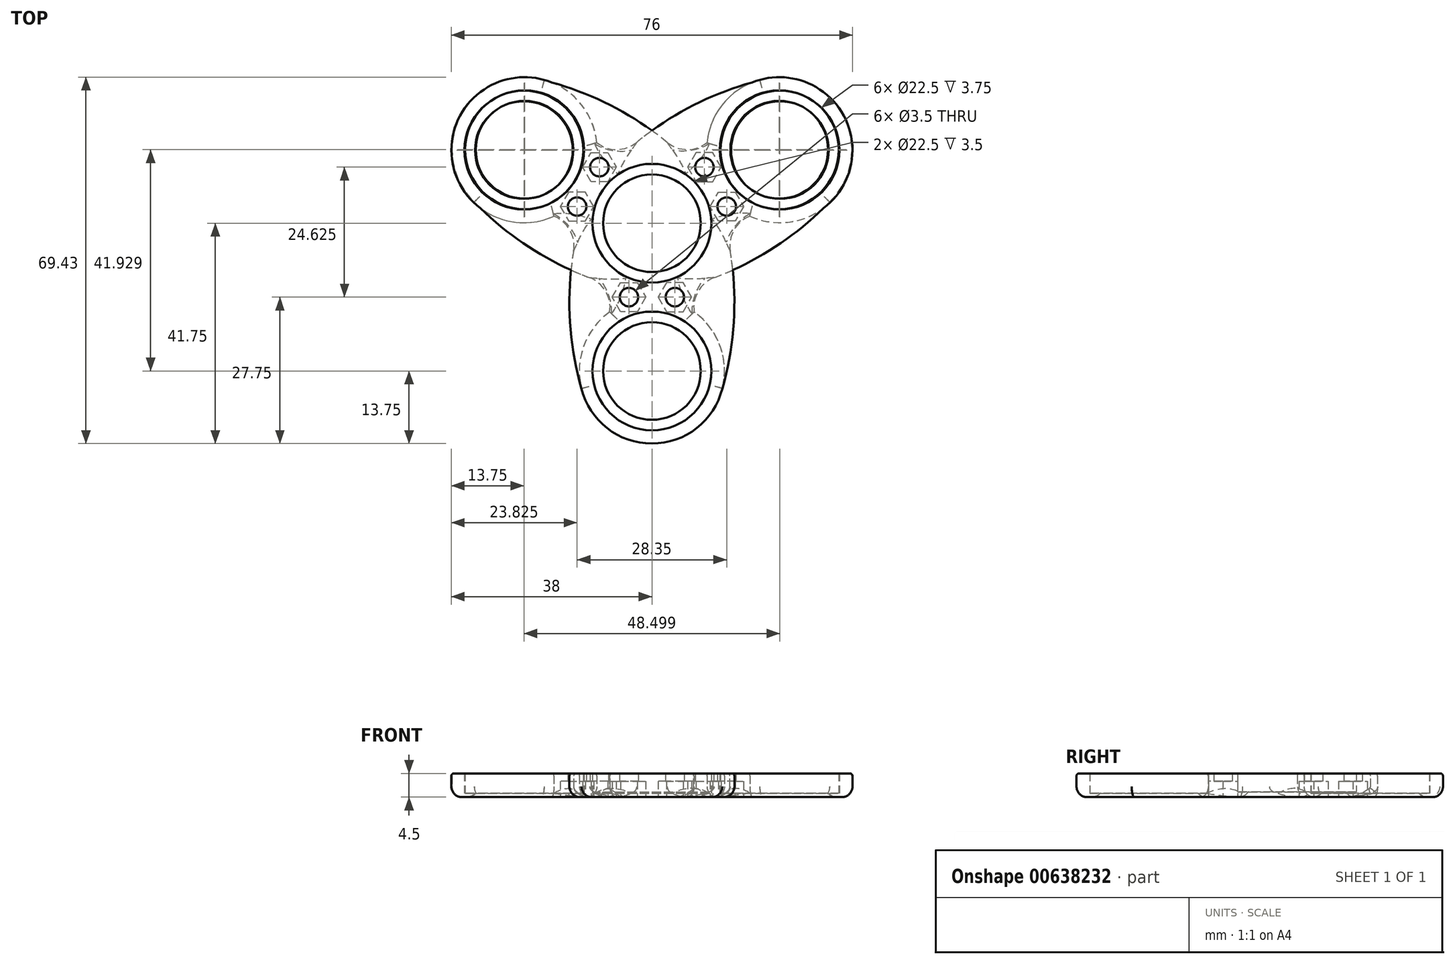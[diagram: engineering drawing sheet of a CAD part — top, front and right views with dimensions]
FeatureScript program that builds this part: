
annotation { "Feature Type Name" : "Feature", "Feature Type Description" : "" }
export const myFeature = defineFeature(function(context is Context, id is Id, definition is map)
    precondition{}
    {
        {
            assignVariable(context, id + "F0", {"name" : "OuterBearingHeight", "anyValue" : 7});
        }
        {
            assignVariable(context, id + "F1", {"name" : "CenterBearingHeight", "anyValue" : 7});
        }
        {
            var Q0;
            Q0=qCreatedBy(makeId("Top.planeOp"),FACE);
            var sketch = newSketch(context, id + "F2", { "sketchPlane" : qUnion([Q0])});
            skCircle(sketch, "E0", {"center": v(0, 0) * mm, "radius": 11.25 * mm});
            skCircle(sketch, "E1", {"center": v(0, 0) * mm, "radius": 9.25 * mm});
            skCircle(sketch, "E2", {"center": v(0, -28) * mm, "radius": 11.25 * mm});
            skCircle(sketch, "E3", {"center": v(0, -28) * mm, "radius": 9.25 * mm});
            skCircle(sketch, "E4", {"center": v(0, 0) * mm, "radius": 13.75 * mm});
            skCircle(sketch, "E5", {"center": v(0, -28) * mm, "radius": 13.75 * mm});
            skArc(sketch, "E6", {"start": v(-13.75, 0) * mm, "mid": v(-15.62, -16.3) * mm, "end": v(-13, -32.48) * mm});
            skArc(sketch, "E7", {"start": v(6.75, -11.98) * mm, "mid": v(7.03, -14.49) * mm, "end": v(8, -16.82) * mm});
            skPoint(sketch, "E8.center", {"position": v(0.04, 0.07) * mm});
            skCircle(sketch, "E9.cCircle", {"center": v(-4.35, -14) * mm, "radius": 2.75 * mm, "construction": true});
            skLineSegment(sketch, "E9.0", {"start": v(-2.76, -16.75) * mm, "end": v(-5.94, -16.75) * mm});
            skLineSegment(sketch, "E9.1", {"start": v(-5.94, -16.75) * mm, "end": v(-7.53, -14) * mm});
            skLineSegment(sketch, "E9.2", {"start": v(-7.53, -14) * mm, "end": v(-5.94, -11.25) * mm});
            skLineSegment(sketch, "E9.3", {"start": v(-5.94, -11.25) * mm, "end": v(-2.76, -11.25) * mm});
            skLineSegment(sketch, "E9.4", {"start": v(-2.76, -11.25) * mm, "end": v(-1.18, -14) * mm});
            skLineSegment(sketch, "E9.5", {"start": v(-1.18, -14) * mm, "end": v(-2.76, -16.75) * mm});
            skPoint(sketch, "E9.0.midPoint", {"position": v(-4.35, -16.75) * mm});
            skLineSegment(sketch, "E10", {"start": v(-4.35, -14) * mm, "end": v(-4.35, -13.04) * mm, "construction": true});
            skLineSegment(sketch, "E11", {"start": v(-4.35, -14) * mm, "end": v(-4.35, -14.96) * mm, "construction": true});
            skLineSegment(sketch, "E12", {"start": v(-4.35, -14) * mm, "end": v(-15.62, -14) * mm, "construction": true});
            skLineSegment(sketch, "E13", {"start": v(-4.35, -14) * mm, "end": v(6.92, -14) * mm, "construction": true});
            skCircle(sketch, "E14", {"center": v(-4.35, -14) * mm, "radius": 1.75 * mm});
            skArc(sketch, "E15.1.0", {"start": v(6.87, 11.76) * mm, "mid": v(8.9, 13.26) * mm, "end": v(10.44, 15.27) * mm});
            skCircle(sketch, "E15.1.1", {"center": v(24.12, 13.93) * mm, "radius": 13.75 * mm});
            skCircle(sketch, "E15.1.2", {"center": v(24.12, 13.93) * mm, "radius": 11.25 * mm});
            skCircle(sketch, "E15.1.3", {"center": v(24.12, 13.93) * mm, "radius": 9.25 * mm});
            skArc(sketch, "E15.1.4", {"start": v(6.75, -11.98) * mm, "mid": v(21.8, -5.45) * mm, "end": v(34.5, 4.9) * mm});
            skLineSegment(sketch, "E15.1.5", {"start": v(12.59, 5.91) * mm, "end": v(15.76, 5.91) * mm});
            skLineSegment(sketch, "E15.1.6", {"start": v(11, 3.16) * mm, "end": v(12.59, 5.91) * mm});
            skLineSegment(sketch, "E15.1.7", {"start": v(12.59, 0.41) * mm, "end": v(11, 3.16) * mm});
            skLineSegment(sketch, "E15.1.8", {"start": v(15.76, 0.41) * mm, "end": v(12.59, 0.41) * mm});
            skLineSegment(sketch, "E15.1.9", {"start": v(17.35, 3.16) * mm, "end": v(15.76, 0.41) * mm});
            skLineSegment(sketch, "E15.1.10", {"start": v(15.76, 5.91) * mm, "end": v(17.35, 3.16) * mm});
            skCircle(sketch, "E15.1.11", {"center": v(14.18, 3.16) * mm, "radius": 1.75 * mm});
            skArc(sketch, "E15.2.0", {"start": v(-13.75, 0) * mm, "mid": v(-16.06, 1) * mm, "end": v(-18.56, 1.34) * mm});
            skCircle(sketch, "E15.2.1", {"center": v(-24.25, 13.86) * mm, "radius": 13.75 * mm});
            skCircle(sketch, "E15.2.2", {"center": v(-24.25, 13.86) * mm, "radius": 11.25 * mm});
            skCircle(sketch, "E15.2.3", {"center": v(-24.25, 13.86) * mm, "radius": 9.25 * mm});
            skArc(sketch, "E15.2.4", {"start": v(6.87, 11.76) * mm, "mid": v(-6.3, 21.52) * mm, "end": v(-21.63, 27.35) * mm});
            skLineSegment(sketch, "E15.2.5", {"start": v(-11.54, 7.87) * mm, "end": v(-13.12, 10.62) * mm});
            skLineSegment(sketch, "E15.2.6", {"start": v(-8.36, 7.87) * mm, "end": v(-11.54, 7.87) * mm});
            skLineSegment(sketch, "E15.2.7", {"start": v(-6.77, 10.62) * mm, "end": v(-8.36, 7.87) * mm});
            skLineSegment(sketch, "E15.2.8", {"start": v(-8.36, 13.37) * mm, "end": v(-6.77, 10.62) * mm});
            skLineSegment(sketch, "E15.2.9", {"start": v(-11.54, 13.37) * mm, "end": v(-8.36, 13.37) * mm});
            skLineSegment(sketch, "E15.2.10", {"start": v(-13.12, 10.62) * mm, "end": v(-11.54, 13.37) * mm});
            skCircle(sketch, "E15.2.11", {"center": v(-9.95, 10.62) * mm, "radius": 1.75 * mm});
            skPoint(sketch, "E15.center", {"position": v(-0.04, -0.07) * mm});
            skSolve(sketch);
        }
        {
            var Q0;
            {var subQ0=sQuery(id+"F2.wireOp",EDGE,"E9.1");Q0=makeQuery(id+"F2.imprint","IMPRINT",FACE,{"disambiguationData":[TD([[makeQuery(id+"F2.imprint","IMPRINT",EDGE,{"derivedFrom":subQ0}),1.0]])]});}
            var Q1;
            {var subQ5=sQuery(id+"F2.wireOp",EDGE,"E7");Q1=makeQuery(id+"F2.imprint","IMPRINT",FACE,{"disambiguationData":[TD([[makeQuery(id+"F2.imprint","IMPRINT",EDGE,{"derivedFrom":subQ5}),-1.0]])]});}
            var Q2;
            {var subQ0=sQuery(id+"F2.wireOp",EDGE,"E15.1.8");Q2=makeQuery(id+"F2.imprint","IMPRINT",FACE,{"disambiguationData":[TD([[makeQuery(id+"F2.imprint","IMPRINT",EDGE,{"derivedFrom":subQ0}),1.0]])]});}
            var Q3;
            Q3=makeQuery(id+"F2.imprint","IMPRINT",FACE,{"disambiguationData":[TD([[makeQuery(id+"F2.imprint","IMPRINT",EDGE,{"derivedFrom":sQuery(id+"F2.wireOp",EDGE,"E0")}),-1.0]])]});
            var Q4;
            {var subQ1=sQuery(id+"F2.wireOp",EDGE,"E15.1.0");Q4=makeQuery(id+"F2.imprint","IMPRINT",FACE,{"disambiguationData":[TD([[makeQuery(id+"F2.imprint","IMPRINT",EDGE,{"derivedFrom":subQ1}),-1.0]])]});}
            var Q5;
            {var subQ0=sQuery(id+"F2.wireOp",EDGE,"E15.2.8");Q5=makeQuery(id+"F2.imprint","IMPRINT",FACE,{"disambiguationData":[TD([[makeQuery(id+"F2.imprint","IMPRINT",EDGE,{"derivedFrom":subQ0}),1.0]])]});}
            var Q6;
            Q6=makeQuery(id+"F2.imprint","IMPRINT",FACE,{"disambiguationData":[TD([[makeQuery(id+"F2.imprint","IMPRINT",EDGE,{"derivedFrom":sQuery(id+"F2.wireOp",EDGE,"E15.2.2")}),-1.0]])]});
            var Q7;
            Q7=makeQuery(id+"F2.imprint","IMPRINT",FACE,{"disambiguationData":[TD([[makeQuery(id+"F2.imprint","IMPRINT",EDGE,{"derivedFrom":sQuery(id+"F2.wireOp",EDGE,"E15.1.2")}),-1.0]])]});
            var Q8;
            {var subQ1=sQuery(id+"F2.wireOp",EDGE,"E15.2.0");Q8=makeQuery(id+"F2.imprint","IMPRINT",FACE,{"disambiguationData":[TD([[makeQuery(id+"F2.imprint","IMPRINT",EDGE,{"derivedFrom":subQ1}),-1.0]])]});}
            var Q9;
            Q9=makeQuery(id+"F2.imprint","IMPRINT",FACE,{"disambiguationData":[TD([[makeQuery(id+"F2.imprint","IMPRINT",EDGE,{"derivedFrom":sQuery(id+"F2.wireOp",EDGE,"E2")}),-1.0]])]});
            var Q10;
            {var subQ0=sQuery(id+"F2.wireOp",EDGE,"E6");var subQ1=sQuery(id+"F2.wireOp",EDGE,"E5");var subQ2=makeQuery(id+"F2.imprint","INTERSECT",VERTEX,{"disambiguationData":[OD(0.0)],"derivedFrom":[subQ1,subQ0]});Q10=makeQuery(id+"F2.imprint","IMPRINT",FACE,{"disambiguationData":[TD([[makeQuery(id+"F2.imprint","IMPRINT",EDGE,{"disambiguationData":[TD([[subQ2,1.0]])],"derivedFrom":subQ1}),1.0]])]});}
            var Q11;
            {var subQ0=sQuery(id+"F2.wireOp",EDGE,"E15.2.4");var subQ1=sQuery(id+"F2.wireOp",EDGE,"E15.2.1");var subQ2=makeQuery(id+"F2.imprint","INTERSECT",VERTEX,{"disambiguationData":[OD(0.0)],"derivedFrom":[subQ1,subQ0]});Q11=makeQuery(id+"F2.imprint","IMPRINT",FACE,{"disambiguationData":[TD([[makeQuery(id+"F2.imprint","IMPRINT",EDGE,{"disambiguationData":[TD([[subQ2,1.0]])],"derivedFrom":subQ1}),1.0]])]});}
            var Q12;
            {var subQ0=sQuery(id+"F2.wireOp",EDGE,"E15.1.4");var subQ1=sQuery(id+"F2.wireOp",EDGE,"E15.1.1");var subQ2=makeQuery(id+"F2.imprint","INTERSECT",VERTEX,{"disambiguationData":[OD(0.0)],"derivedFrom":[subQ1,subQ0]});Q12=makeQuery(id+"F2.imprint","IMPRINT",FACE,{"disambiguationData":[TD([[makeQuery(id+"F2.imprint","IMPRINT",EDGE,{"disambiguationData":[TD([[subQ2,1.0]])],"derivedFrom":subQ1}),1.0]])]});}
            extrude(context, id + "F3", {"entities" : qUnion([Q0, Q1, Q2, Q3, Q4, Q5, Q6, Q7, Q8, Q9, Q10, Q11, Q12]), "depth" : ((getVariable(context, 'CenterBearingHeight') / 2) + 1) * mm, "offsetDistance" : 25 * mm});
        }
        {
            var Q0;
            Q0=makeQuery(id+"F2.imprint","IMPRINT",FACE,{"disambiguationData":[TD([[makeQuery(id+"F2.imprint","IMPRINT",EDGE,{"derivedFrom":sQuery(id+"F2.wireOp",EDGE,"E15.2.2")}),1.0]])]});
            var Q1;
            Q1=makeQuery(id+"F2.imprint","IMPRINT",FACE,{"disambiguationData":[TD([[makeQuery(id+"F2.imprint","IMPRINT",EDGE,{"derivedFrom":sQuery(id+"F2.wireOp",EDGE,"E15.1.2")}),1.0]])]});
            var Q2;
            Q2=makeQuery(id+"F2.imprint","IMPRINT",FACE,{"disambiguationData":[TD([[makeQuery(id+"F2.imprint","IMPRINT",EDGE,{"derivedFrom":sQuery(id+"F2.wireOp",EDGE,"E2")}),1.0]])]});
            extrude(context, id + "F4", {"entities" : qUnion([Q0, Q1, Q2]), "operationType" : NewBodyOperationType.ADD, "depth" : (((getVariable(context, 'CenterBearingHeight') / 2) + .75) - getVariable(context, 'OuterBearingHeight') / 2) * mm, "offsetDistance" : 25 * mm});
        }
        {
            var Q0;
            {var subQ0=sQuery(id+"F2.wireOp",EDGE,"E9.2");var subQ5=sQuery(id+"F2.wireOp",EDGE,"E4");var subQ6=makeQuery(id+"F2.imprint","INTERSECT",VERTEX,{"derivedFrom":[subQ5,subQ0]});Q0=makeQuery(id+"F2.imprint","IMPRINT",FACE,{"disambiguationData":[TD([[makeQuery(id+"F2.imprint","IMPRINT",EDGE,{"disambiguationData":[TD([[subQ6,-1.0]])],"derivedFrom":subQ5}),-1.0]])]});}
            var Q1;
            {var subQ0=sQuery(id+"F2.wireOp",EDGE,"E9.0");Q1=makeQuery(id+"F2.imprint","IMPRINT",FACE,{"disambiguationData":[TD([[makeQuery(id+"F2.imprint","IMPRINT",EDGE,{"derivedFrom":subQ0}),-1.0]])]});}
            var Q2;
            {var subQ1=sQuery(id+"F2.wireOp",EDGE,"E15.2.8");var subQ5=sQuery(id+"F2.wireOp",EDGE,"E4");var subQ6=makeQuery(id+"F2.imprint","INTERSECT",VERTEX,{"derivedFrom":[subQ5,subQ1]});Q2=makeQuery(id+"F2.imprint","IMPRINT",FACE,{"disambiguationData":[TD([[makeQuery(id+"F2.imprint","IMPRINT",EDGE,{"disambiguationData":[TD([[subQ6,-1.0]])],"derivedFrom":subQ5}),-1.0]])]});}
            var Q3;
            {var subQ0=sQuery(id+"F2.wireOp",EDGE,"E15.2.10");Q3=makeQuery(id+"F2.imprint","IMPRINT",FACE,{"disambiguationData":[TD([[makeQuery(id+"F2.imprint","IMPRINT",EDGE,{"derivedFrom":subQ0}),-1.0]])]});}
            var Q4;
            {var subQ5=sQuery(id+"F2.wireOp",EDGE,"E4");var subQ7=sQuery(id+"F2.wireOp",EDGE,"E15.1.11");var subQ9=makeQuery(id+"F2.imprint","INTERSECT",VERTEX,{"disambiguationData":[OD(0.0)],"derivedFrom":[subQ5,subQ7]});Q4=makeQuery(id+"F2.imprint","IMPRINT",FACE,{"disambiguationData":[TD([[makeQuery(id+"F2.imprint","IMPRINT",EDGE,{"disambiguationData":[TD([[subQ9,1.0]])],"derivedFrom":subQ5}),-1.0]])]});}
            var Q5;
            {var subQ0=sQuery(id+"F2.wireOp",EDGE,"E15.1.10");Q5=makeQuery(id+"F2.imprint","IMPRINT",FACE,{"disambiguationData":[TD([[makeQuery(id+"F2.imprint","IMPRINT",EDGE,{"derivedFrom":subQ0}),-1.0]])]});}
            var Q6;
            {var subQ0=sQuery(id+"F2.wireOp",EDGE,"E15.1.7");Q6=makeQuery(id+"F2.imprint","IMPRINT",FACE,{"disambiguationData":[TD([[makeQuery(id+"F2.imprint","IMPRINT",EDGE,{"derivedFrom":subQ0}),-1.0]])]});}
            var Q7;
            {var subQ0=sQuery(id+"F2.wireOp",EDGE,"E15.2.7");Q7=makeQuery(id+"F2.imprint","IMPRINT",FACE,{"disambiguationData":[TD([[makeQuery(id+"F2.imprint","IMPRINT",EDGE,{"derivedFrom":subQ0}),-1.0]])]});}
            var Q8;
            {var subQ5=sQuery(id+"F2.wireOp",EDGE,"E15.2.11");var subQ7=sQuery(id+"F2.wireOp",EDGE,"E4");var subQ9=makeQuery(id+"F2.imprint","INTERSECT",VERTEX,{"disambiguationData":[OD(1.0)],"derivedFrom":[subQ7,subQ5]});Q8=makeQuery(id+"F2.imprint","IMPRINT",FACE,{"disambiguationData":[TD([[makeQuery(id+"F2.imprint","IMPRINT",EDGE,{"disambiguationData":[TD([[subQ9,-1.0]])],"derivedFrom":subQ7}),-1.0]])]});}
            var Q9;
            {var subQ3=sQuery(id+"F2.wireOp",EDGE,"E4");var subQ7=sQuery(id+"F2.wireOp",EDGE,"E15.1.11");var subQ9=makeQuery(id+"F2.imprint","INTERSECT",VERTEX,{"disambiguationData":[OD(1.0)],"derivedFrom":[subQ3,subQ7]});Q9=makeQuery(id+"F2.imprint","IMPRINT",FACE,{"disambiguationData":[TD([[makeQuery(id+"F2.imprint","IMPRINT",EDGE,{"disambiguationData":[TD([[subQ9,-1.0]])],"derivedFrom":subQ3}),-1.0]])]});}
            var Q10;
            {var subQ0=sQuery(id+"F2.wireOp",EDGE,"E9.3");Q10=makeQuery(id+"F2.imprint","IMPRINT",FACE,{"disambiguationData":[TD([[makeQuery(id+"F2.imprint","IMPRINT",EDGE,{"derivedFrom":subQ0}),-1.0]])]});}
            var Q11;
            {var subQ5=sQuery(id+"F2.wireOp",EDGE,"E14");var subQ7=sQuery(id+"F2.wireOp",EDGE,"E4");var subQ8=makeQuery(id+"F2.imprint","INTERSECT",VERTEX,{"disambiguationData":[OD(1.0)],"derivedFrom":[subQ7,subQ5]});Q11=makeQuery(id+"F2.imprint","IMPRINT",FACE,{"disambiguationData":[TD([[makeQuery(id+"F2.imprint","IMPRINT",EDGE,{"disambiguationData":[TD([[subQ8,-1.0]])],"derivedFrom":subQ7}),-1.0]])]});}
            extrude(context, id + "F5", {"entities" : qUnion([Q0, Q1, Q2, Q3, Q4, Q5, Q6, Q7, Q8, Q9, Q10, Q11]), "operationType" : NewBodyOperationType.ADD, "depth" : ((getVariable(context, 'CenterBearingHeight') / 2) + 1) * mm, "offsetDistance" : 25 * mm, "hasSecondDirection" : true, "secondDirectionOppositeDirection" : false, "secondDirectionDepth" : 3 * mm});
        }
        {
            var Q0;
            Q0=makeQuery(id+"F2.imprint","IMPRINT",FACE,{"disambiguationData":[TD([[makeQuery(id+"F2.imprint","IMPRINT",EDGE,{"derivedFrom":sQuery(id+"F2.wireOp",EDGE,"E0")}),1.0]])]});
            extrude(context, id + "F6", {"entities" : qUnion([Q0]), "operationType" : NewBodyOperationType.ADD, "depth" : 1 * mm, "offsetDistance" : 25 * mm});
        }
        {
            var Q0;
            Q0=makeQuery(id+"F3.opExtrude","CAP_EDGE",EDGE,{"disambiguationData":[OSD([sQuery(id+"F2.wireOp",EDGE,"E15.1.1")])],"isStart":true});
            var Q1;
            Q1=makeQuery(id+"F3.opExtrude","CAP_EDGE",EDGE,{"disambiguationData":[OSD([sQuery(id+"F2.wireOp",EDGE,"E15.1.4")])],"isStart":true});
            var Q2;
            Q2=makeQuery(id+"F3.opExtrude","CAP_EDGE",EDGE,{"disambiguationData":[OSD([sQuery(id+"F2.wireOp",EDGE,"E7")])],"isStart":true});
            var Q3;
            Q3=makeQuery(id+"F3.opExtrude","CAP_EDGE",EDGE,{"disambiguationData":[OSD([sQuery(id+"F2.wireOp",EDGE,"E5")])],"isStart":true});
            var Q4;
            Q4=makeQuery(id+"F3.opExtrude","CAP_EDGE",EDGE,{"disambiguationData":[OSD([sQuery(id+"F2.wireOp",EDGE,"E6")])],"isStart":true});
            var Q5;
            Q5=makeQuery(id+"F3.opExtrude","CAP_EDGE",EDGE,{"disambiguationData":[OSD([sQuery(id+"F2.wireOp",EDGE,"E15.2.0")])],"isStart":true});
            var Q6;
            Q6=makeQuery(id+"F3.opExtrude","CAP_EDGE",EDGE,{"disambiguationData":[OSD([sQuery(id+"F2.wireOp",EDGE,"E15.2.1")])],"isStart":true});
            var Q7;
            Q7=makeQuery(id+"F3.opExtrude","CAP_EDGE",EDGE,{"disambiguationData":[OSD([sQuery(id+"F2.wireOp",EDGE,"E15.2.4")])],"isStart":true});
            var Q8;
            Q8=makeQuery(id+"F3.opExtrude","CAP_EDGE",EDGE,{"disambiguationData":[OSD([sQuery(id+"F2.wireOp",EDGE,"E15.1.0")])],"isStart":true});
            var Q9;
            {var subQ0=sQuery(id+"F2.wireOp",EDGE,"E4");Q9=makeQuery(id+"F3.opExtrude","CAP_EDGE",EDGE,{"disambiguationData":[OSD([subQ0]),TDD([makeQuery(id+"F2.imprint","IMPRINT",EDGE,{"disambiguationData":[TD([[makeQuery(id+"F2.imprint","INTERSECT",VERTEX,{"derivedFrom":[subQ0,sQuery(id+"F2.wireOp",EDGE,"E15.1.0")]}),-1.0]])],"derivedFrom":subQ0})])],"isStart":true});}
            var Q10;
            {var subQ0=sQuery(id+"F2.wireOp",EDGE,"E4");Q10=makeQuery(id+"F3.opExtrude","CAP_EDGE",EDGE,{"disambiguationData":[OSD([subQ0]),TDD([makeQuery(id+"F2.imprint","IMPRINT",EDGE,{"disambiguationData":[TD([[makeQuery(id+"F2.imprint","INTERSECT",VERTEX,{"derivedFrom":[subQ0,sQuery(id+"F2.wireOp",EDGE,"E6")]}),1.0]])],"derivedFrom":subQ0})])],"isStart":true});}
            var Q11;
            {var subQ0=sQuery(id+"F2.wireOp",EDGE,"E4");Q11=makeQuery(id+"F3.opExtrude","CAP_EDGE",EDGE,{"disambiguationData":[OSD([subQ0]),TDD([makeQuery(id+"F2.imprint","IMPRINT",EDGE,{"disambiguationData":[TD([[makeQuery(id+"F2.imprint","INTERSECT",VERTEX,{"derivedFrom":[subQ0,sQuery(id+"F2.wireOp",EDGE,"E7")]}),-1.0]])],"derivedFrom":subQ0})])],"isStart":true});}
            fillet(context, id + "F7", {"entities" : qUnion([Q0, Q1, Q2, Q3, Q4, Q5, Q6, Q7, Q8, Q9, Q10, Q11]), "radius" : 2 * mm, "tangentPropagation" : true, "allowEdgeOverflow" : false});
        }
        {
            var Q0;
            Q0=makeQuery(id+"F4.opExtrude","CAP_EDGE",EDGE,{"disambiguationData":[OSD([sQuery(id+"F2.wireOp",EDGE,"E15.2.3")])],"isStart":true});
            var Q1;
            Q1=makeQuery(id+"F6.opExtrude","CAP_EDGE",EDGE,{"disambiguationData":[OSD([sQuery(id+"F2.wireOp",EDGE,"E1")])],"isStart":true});
            var Q2;
            Q2=makeQuery(id+"F4.opExtrude","CAP_EDGE",EDGE,{"disambiguationData":[OSD([sQuery(id+"F2.wireOp",EDGE,"E3")])],"isStart":true});
            var Q3;
            Q3=makeQuery(id+"F4.opExtrude","CAP_EDGE",EDGE,{"disambiguationData":[OSD([sQuery(id+"F2.wireOp",EDGE,"E15.1.3")])],"isStart":true});
            fillet(context, id + "F8", {"entities" : qUnion([Q0, Q1, Q2, Q3]), "radius" : 2 * mm, "tangentPropagation" : true, "allowEdgeOverflow" : false});
        }
        {
            var Q0;
            Q0=makeQuery(id+"F3.opExtrude","SWEPT_EDGE",EDGE,{"disambiguationData":[OSD([sQuery(id+"F2.wireOp",EDGE,"E4"),sQuery(id+"F2.wireOp",EDGE,"E6"),sQuery(id+"F2.wireOp",EDGE,"E15.2.0")])]});
            var Q1;
            Q1=makeQuery(id+"F3.opExtrude","SWEPT_EDGE",EDGE,{"disambiguationData":[OSD([sQuery(id+"F2.wireOp",EDGE,"E4"),sQuery(id+"F2.wireOp",EDGE,"E7"),sQuery(id+"F2.wireOp",EDGE,"E15.1.4")])]});
            var Q2;
            Q2=makeQuery(id+"F3.opExtrude","SWEPT_EDGE",EDGE,{"disambiguationData":[OSD([sQuery(id+"F2.wireOp",EDGE,"E15.1.0"),sQuery(id+"F2.wireOp",EDGE,"E15.2.4")])]});
            fillet(context, id + "F9", {"entities" : qUnion([Q0, Q1, Q2]), "radius" : 6 * mm, "tangentPropagation" : true, "allowEdgeOverflow" : false});
        }
        {
            var Q0;
            Q0=makeQuery(id+"F3.opExtrude","SWEPT_EDGE",EDGE,{"disambiguationData":[OSD([sQuery(id+"F2.wireOp",EDGE,"E5"),sQuery(id+"F2.wireOp",EDGE,"E6")])]});
            var Q1;
            Q1=makeQuery(id+"F3.opExtrude","SWEPT_EDGE",EDGE,{"disambiguationData":[OSD([sQuery(id+"F2.wireOp",EDGE,"E15.2.1"),sQuery(id+"F2.wireOp",EDGE,"E15.2.4")])]});
            var Q2;
            Q2=makeQuery(id+"F3.opExtrude","SWEPT_EDGE",EDGE,{"disambiguationData":[OSD([sQuery(id+"F2.wireOp",EDGE,"E15.1.1"),sQuery(id+"F2.wireOp",EDGE,"E15.1.4")])]});
            var Q3;
            Q3=makeQuery(id+"F3.opExtrude","CAP_EDGE",EDGE,{"disambiguationData":[OSD([sQuery(id+"F2.wireOp",EDGE,"E5")])],"isStart":false});
            var Q4;
            Q4=makeQuery(id+"F3.opExtrude","CAP_EDGE",EDGE,{"disambiguationData":[OSD([sQuery(id+"F2.wireOp",EDGE,"E6")])],"isStart":false});
            var Q5;
            Q5=makeQuery(id+"F3.opExtrude","CAP_EDGE",EDGE,{"disambiguationData":[OSD([sQuery(id+"F2.wireOp",EDGE,"E15.1.4")])],"isStart":false});
            var Q6;
            Q6=makeQuery(id+"F3.opExtrude","CAP_EDGE",EDGE,{"disambiguationData":[OSD([sQuery(id+"F2.wireOp",EDGE,"E15.1.1")])],"isStart":false});
            var Q7;
            Q7=makeQuery(id+"F3.opExtrude","CAP_EDGE",EDGE,{"disambiguationData":[OSD([sQuery(id+"F2.wireOp",EDGE,"E15.2.4")])],"isStart":false});
            var Q8;
            Q8=makeQuery(id+"F3.opExtrude","CAP_EDGE",EDGE,{"disambiguationData":[OSD([sQuery(id+"F2.wireOp",EDGE,"E15.2.1")])],"isStart":false});
            fillet(context, id + "F10", {"entities" : qUnion([Q0, Q1, Q2, Q3, Q4, Q5, Q6, Q7, Q8]), "radius" : .5 * mm, "tangentPropagation" : true, "allowEdgeOverflow" : false});
        }
        {
            var Q0;
            Q0=makeQuery(id+"F3.opExtrude","SWEPT_BODY",BODY,{"disambiguationData":[OSD([sQuery(id+"F2.wireOp",EDGE,"E0"),sQuery(id+"F2.wireOp",EDGE,"E2"),sQuery(id+"F2.wireOp",EDGE,"E4"),sQuery(id+"F2.wireOp",EDGE,"E5"),sQuery(id+"F2.wireOp",EDGE,"E6"),sQuery(id+"F2.wireOp",EDGE,"E7"),sQuery(id+"F2.wireOp",EDGE,"E9.0"),sQuery(id+"F2.wireOp",EDGE,"E9.1"),sQuery(id+"F2.wireOp",EDGE,"E9.2"),sQuery(id+"F2.wireOp",EDGE,"E9.3"),sQuery(id+"F2.wireOp",EDGE,"E9.4"),sQuery(id+"F2.wireOp",EDGE,"E9.5"),sQuery(id+"F2.wireOp",EDGE,"E15.1.0"),sQuery(id+"F2.wireOp",EDGE,"E15.1.1"),sQuery(id+"F2.wireOp",EDGE,"E15.1.2"),sQuery(id+"F2.wireOp",EDGE,"E15.1.4"),sQuery(id+"F2.wireOp",EDGE,"E15.1.5"),sQuery(id+"F2.wireOp",EDGE,"E15.1.6"),sQuery(id+"F2.wireOp",EDGE,"E15.1.7"),sQuery(id+"F2.wireOp",EDGE,"E15.1.8"),sQuery(id+"F2.wireOp",EDGE,"E15.1.9"),sQuery(id+"F2.wireOp",EDGE,"E15.1.10"),sQuery(id+"F2.wireOp",EDGE,"E15.2.0"),sQuery(id+"F2.wireOp",EDGE,"E15.2.1"),sQuery(id+"F2.wireOp",EDGE,"E15.2.2"),sQuery(id+"F2.wireOp",EDGE,"E15.2.4"),sQuery(id+"F2.wireOp",EDGE,"E15.2.5"),sQuery(id+"F2.wireOp",EDGE,"E15.2.6"),sQuery(id+"F2.wireOp",EDGE,"E15.2.7"),sQuery(id+"F2.wireOp",EDGE,"E15.2.8"),sQuery(id+"F2.wireOp",EDGE,"E15.2.9"),sQuery(id+"F2.wireOp",EDGE,"E15.2.10")])]});
            var Q1;
            Q1=qCreatedBy(makeId("Right.planeOp"),FACE);
            mirror(context, id + "F11", {"entities" : qUnion([Q0]), "mirrorPlane" : qUnion([Q1])});
        }
    });
